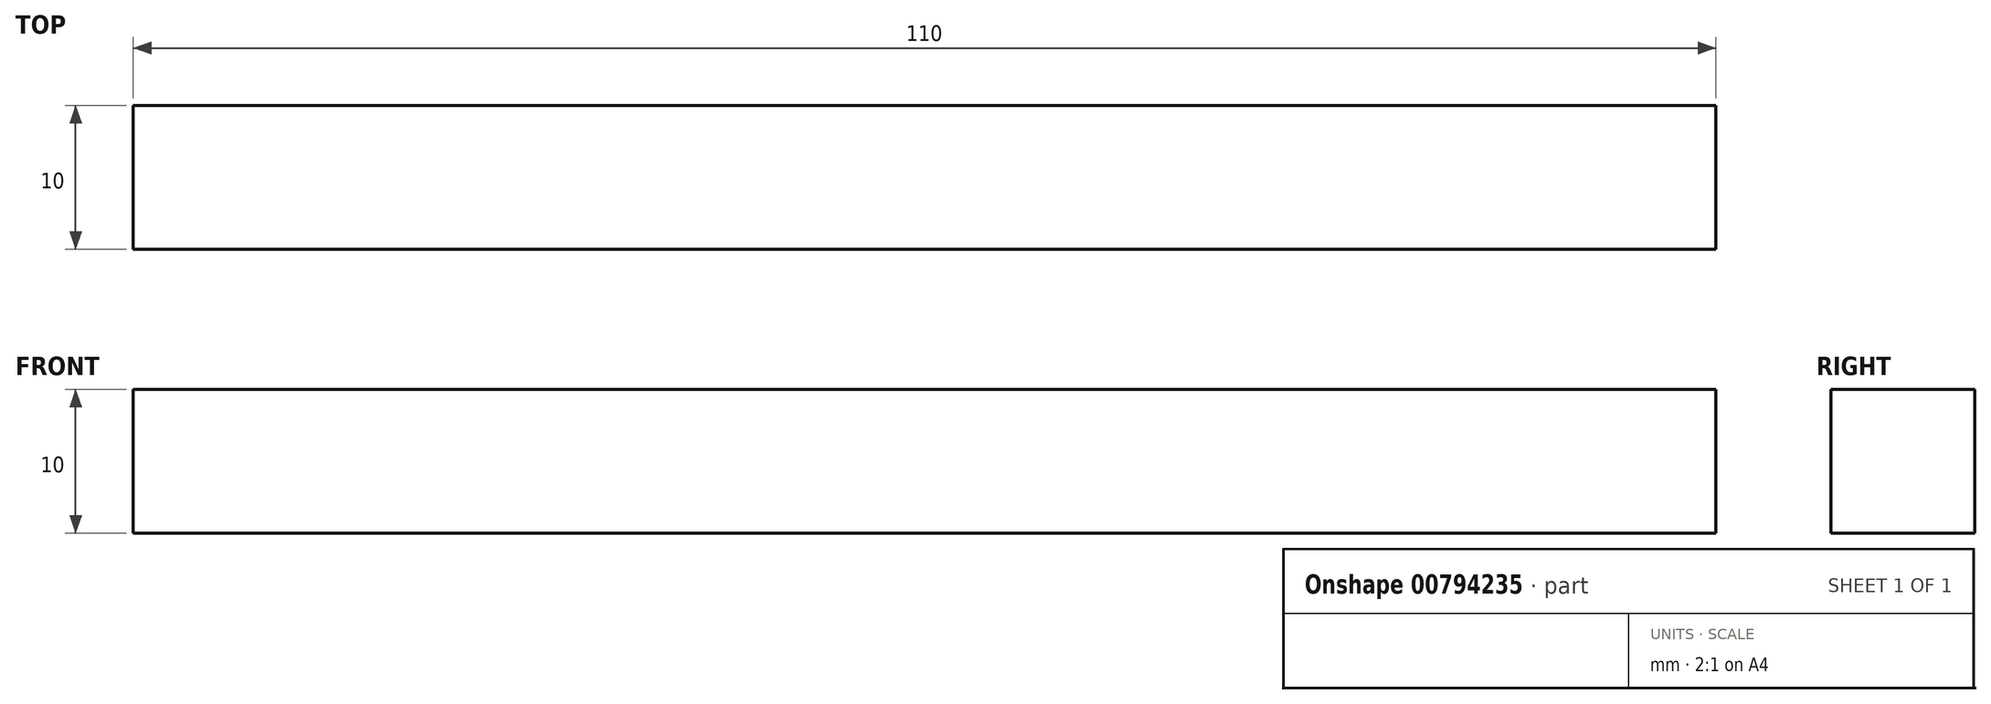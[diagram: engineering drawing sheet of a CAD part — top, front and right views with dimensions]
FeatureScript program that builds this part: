
annotation { "Feature Type Name" : "Feature", "Feature Type Description" : "" }
export const myFeature = defineFeature(function(context is Context, id is Id, definition is map)
    precondition{}
    {
        {
            var Q0;
            Q0=qCreatedBy(makeId("Front.planeOp"),FACE);
            var sketch = newSketch(context, id + "F0", { "sketchPlane" : qUnion([Q0])});
            skLineSegment(sketch, "E0.bottom", {"start": v(-50.37, 10) * mm, "end": v(59.63, 10) * mm});
            skLineSegment(sketch, "E0.top", {"start": v(-50.37, 0) * mm, "end": v(59.63, 0) * mm});
            skLineSegment(sketch, "E0.left", {"start": v(-50.37, 10) * mm, "end": v(-50.37, 0) * mm});
            skLineSegment(sketch, "E0.right", {"start": v(59.63, 10) * mm, "end": v(59.63, 0) * mm});
            skSolve(sketch);
        }
        {
            var Q0;
            Q0=makeQuery(id+"F0.imprint","IMPRINT",FACE,{"disambiguationData":[TD([[makeQuery(id+"F0.imprint","IMPRINT",EDGE,{"derivedFrom":sQuery(id+"F0.wireOp",EDGE,"E0.bottom")}),-1.0]])]});
            extrude(context, id + "F1", {"entities" : qUnion([Q0]), "depth" : 10 * mm, "offsetDistance" : 25 * mm});
        }
    });
